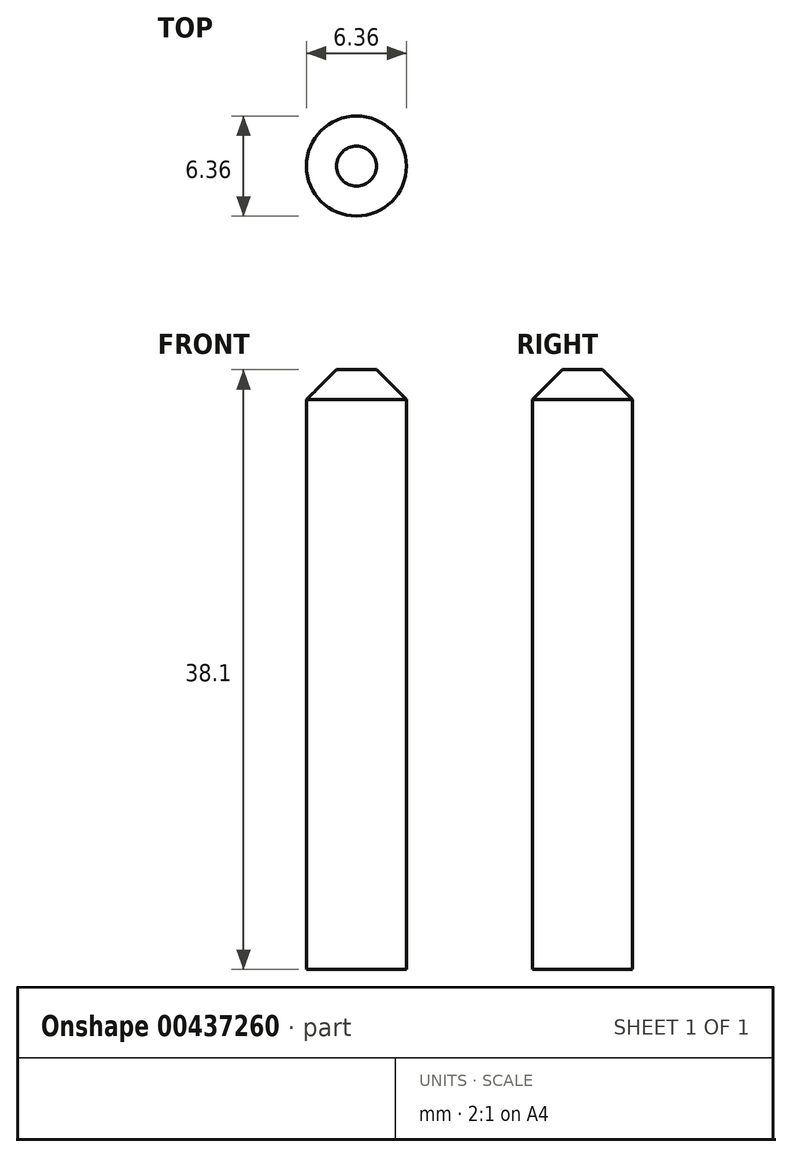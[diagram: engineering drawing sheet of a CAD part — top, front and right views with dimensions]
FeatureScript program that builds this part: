
annotation { "Feature Type Name" : "Feature", "Feature Type Description" : "" }
export const myFeature = defineFeature(function(context is Context, id is Id, definition is map)
    precondition{}
    {
        {
            var Q0;
            Q0=qCreatedBy(makeId("Right.planeOp"),FACE);
            var sketch = newSketch(context, id + "F0", { "sketchPlane" : qUnion([Q0])});
            skLineSegment(sketch, "E0", {"start": v(0, -18.1) * mm, "end": v(0, 18.1) * mm});
            skLineSegment(sketch, "E1", {"start": v(0, -18.1) * mm, "end": v(3.18, -18.1) * mm});
            skLineSegment(sketch, "E2", {"start": v(3.18, -18.1) * mm, "end": v(3.18, 18.1) * mm});
            skLineSegment(sketch, "E3", {"start": v(3.18, 18.1) * mm, "end": v(1.27, 20) * mm});
            skLineSegment(sketch, "E4", {"start": v(1.27, 20) * mm, "end": v(0, 20) * mm});
            skLineSegment(sketch, "E5", {"start": v(0, 20) * mm, "end": v(0, 18.1) * mm});
            skLineSegment(sketch, "E6", {"start": v(3.18, 18.1) * mm, "end": v(0, 18.1) * mm, "construction": true});
            skSolve(sketch);
        }
        {
            var Q0;
            Q0=makeQuery(id+"F0.imprint","IMPRINT",FACE,{"disambiguationData":[TD([[makeQuery(id+"F0.imprint","IMPRINT",EDGE,{"derivedFrom":sQuery(id+"F0.wireOp",EDGE,"E0")}),-1.0]])]});
            var Q1;
            Q1=sQuery(id+"F0.wireOp",EDGE,"E0");
            revolve(context, id + "F1", {"entities" : qUnion([Q0]), "axis" : qUnion([Q1]), "revolveType" : RevolveType.FULL});
        }
    });
